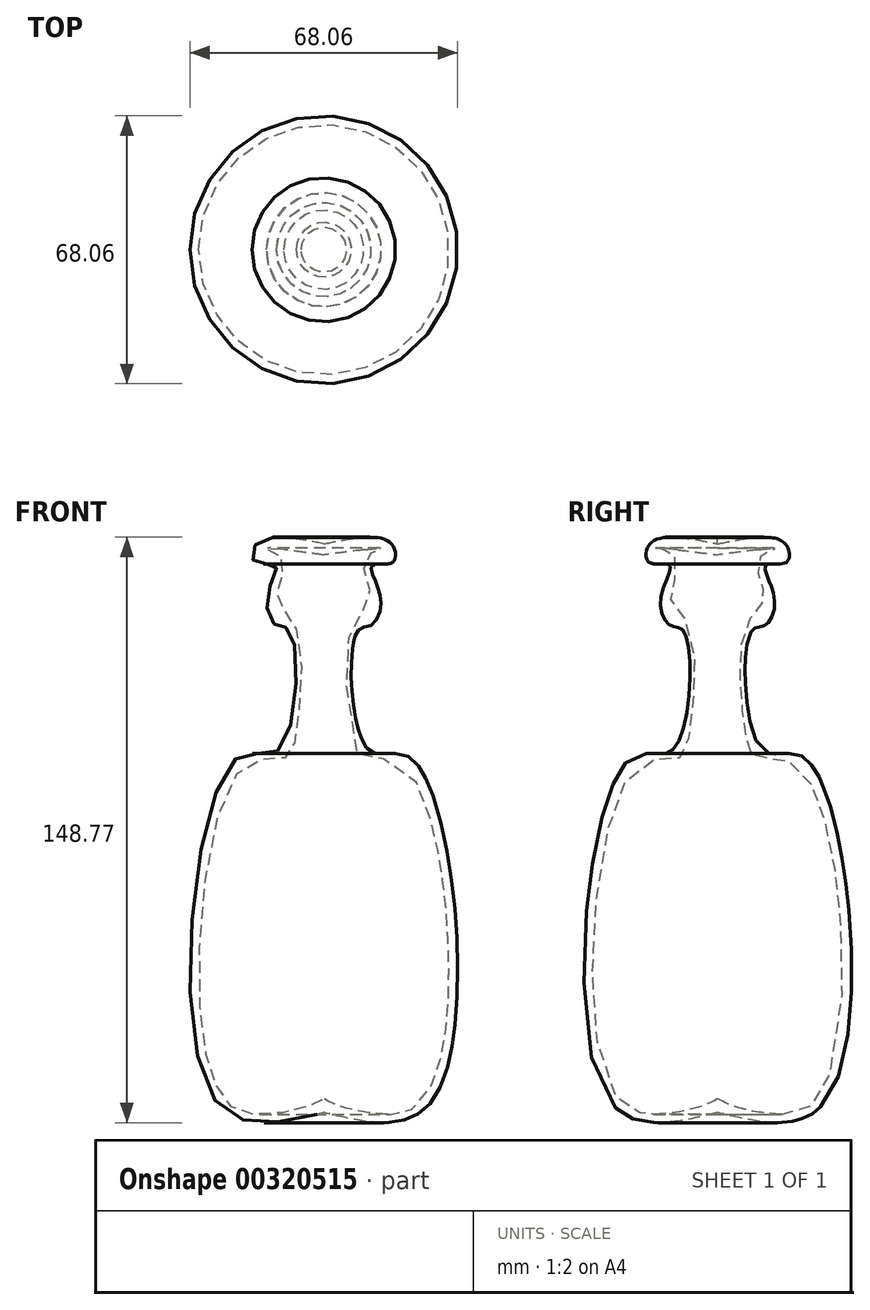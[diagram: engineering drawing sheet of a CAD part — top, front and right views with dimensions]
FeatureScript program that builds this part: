
annotation { "Feature Type Name" : "Feature", "Feature Type Description" : "" }
export const myFeature = defineFeature(function(context is Context, id is Id, definition is map)
    precondition{}
    {
        {
            var Q0;
            Q0=qCreatedBy(makeId("Front.planeOp"),FACE);
            var sketch = newSketch(context, id + "F0", { "sketchPlane" : qUnion([Q0])});
            skFitSpline(sketch, "E0", {"points": [v(0, 70.83) * mm, v(-16.94, 71.07) * mm, v(-17.41, 66.13) * mm, v(-12.24, 65.42) * mm, v(-14.35, 57.42) * mm, v(-12, 50.12) * mm, v(-8.47, 48.48) * mm, v(-11.3, 18.6) * mm, v(-22.36, 16.24) * mm, v(-28.94, -68.48) * mm, v(0, -73.66) * mm], "startDerivative": vector(-204.66, 41.73) * mm, "endDerivative": vector(253.23, 62.07) * mm});
            skFitSpline(sketch, "E1", {"points": [v(0, 68) * mm, v(-7.07, 68.95) * mm, v(-14.6, 69.66) * mm, v(-10.82, 67.54) * mm, v(-11.06, 61.18) * mm, v(-11.77, 56.48) * mm, v(-7.07, 49.42) * mm, v(-7.07, 22.83) * mm, v(-9.88, 16.47) * mm, v(-20.24, 14.35) * mm, v(-31.77, -40.71) * mm, v(-26.12, -69.19) * mm, v(-19.06, -73.9) * mm, v(-4.7, -72.24) * mm, v(0, -70.13) * mm], "startDerivative": vector(-106.87, 14.73) * mm, "endDerivative": vector(79.21, 45.17) * mm});
            skLineSegment(sketch, "E2", {"start": v(0, 76.24) * mm, "end": v(0, 68) * mm});
            skLineSegment(sketch, "E3.trimOffspring", {"start": v(0, -70.13) * mm, "end": v(0, -77.19) * mm});
            skLineSegment(sketch, "E4", {"start": v(-13, 72.5) * mm, "end": v(-10.38, 69.36) * mm});
            skPoint(sketch, "E5.orphan", {"position": v(-14.6, 74.4) * mm});
            skPoint(sketch, "E6.orphan", {"position": v(-7.07, 65.4) * mm});
            skSolve(sketch);
        }
        {
            var Q0;
            {var subQ0=sQuery(id+"F0.wireOp",EDGE,"E0");Q0=makeQuery(id+"F0.imprint","IMPRINT",FACE,{"disambiguationData":[TD([[makeQuery(id+"F0.imprint","IMPRINT",EDGE,{"derivedFrom":subQ0}),1.0]])]});}
            var Q1;
            Q1=sQuery(id+"F0.wireOp",EDGE,"E3.trimOffspring");
            revolve(context, id + "F1", {"entities" : qUnion([Q0]), "axis" : qUnion([Q1]), "revolveType" : RevolveType.FULL});
        }
    });
